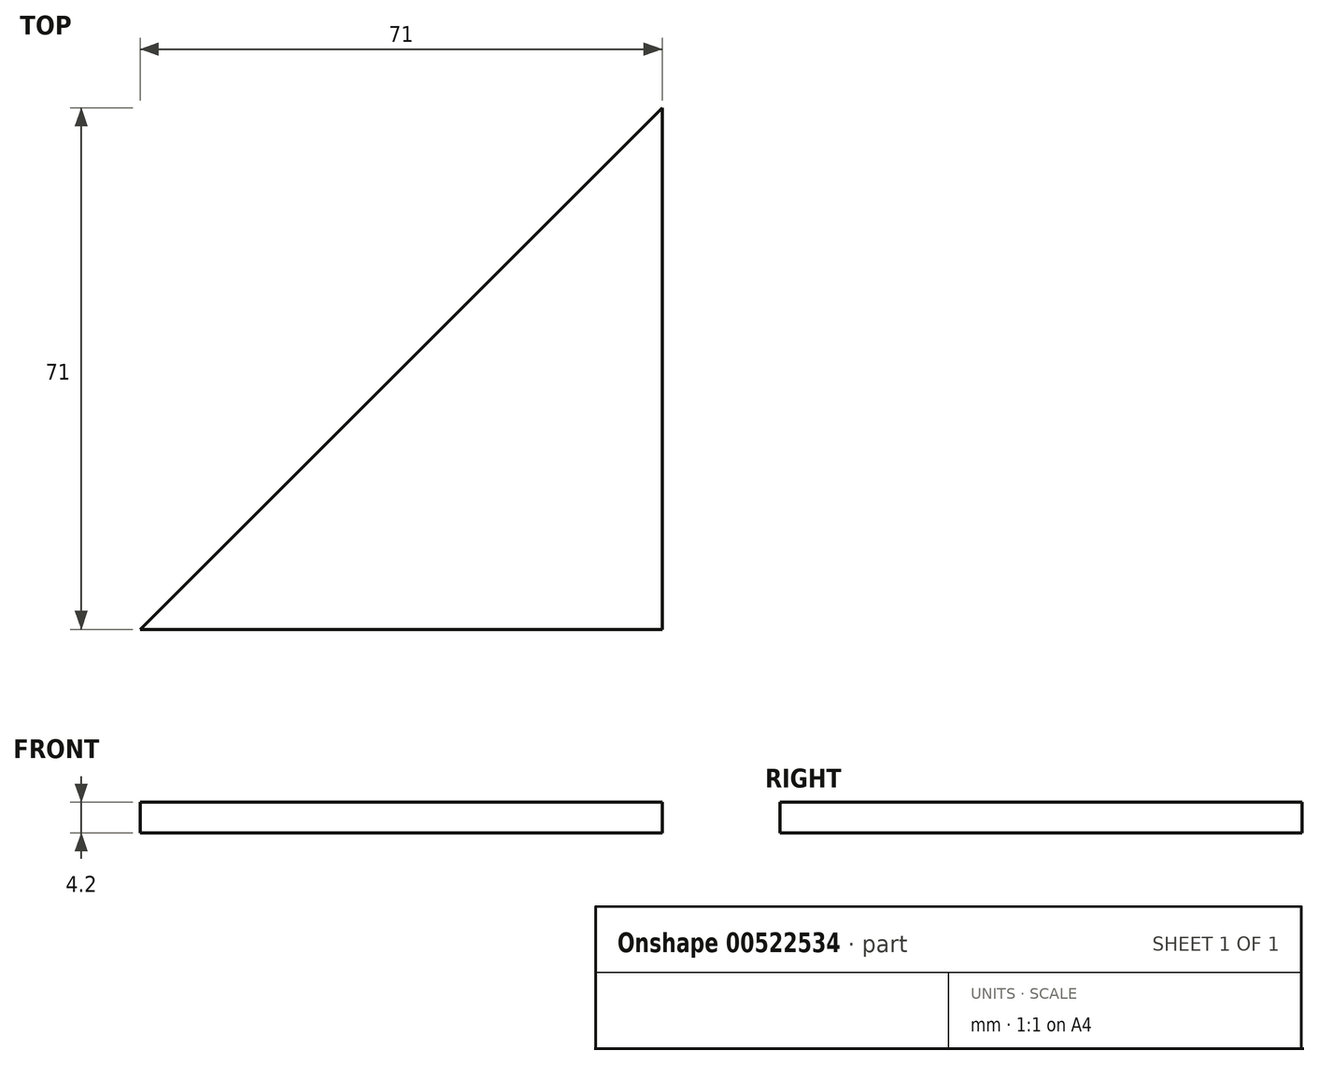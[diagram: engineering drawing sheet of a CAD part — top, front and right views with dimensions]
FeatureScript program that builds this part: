
annotation { "Feature Type Name" : "Feature", "Feature Type Description" : "" }
export const myFeature = defineFeature(function(context is Context, id is Id, definition is map)
    precondition{}
    {
        {
            var Q0;
            Q0=qCreatedBy(makeId("Top.planeOp"),FACE);
            var sketch = newSketch(context, id + "F0", { "sketchPlane" : qUnion([Q0])});
            skLineSegment(sketch, "E0", {"start": v(0, 0) * mm, "end": v(0, 71) * mm});
            skLineSegment(sketch, "E1", {"start": v(0, 71) * mm, "end": v(-71, 0) * mm});
            skLineSegment(sketch, "E2", {"start": v(-71, 0) * mm, "end": v(0, 0) * mm});
            skSolve(sketch);
        }
        {
            var Q0;
            Q0 = qSketchRegion(id + "F0", true);
            extrude(context, id + "F1", {"entities" : qUnion([Q0]), "depth" : 4.2 * mm, "offsetDistance" : 25 * mm});
        }
    });
